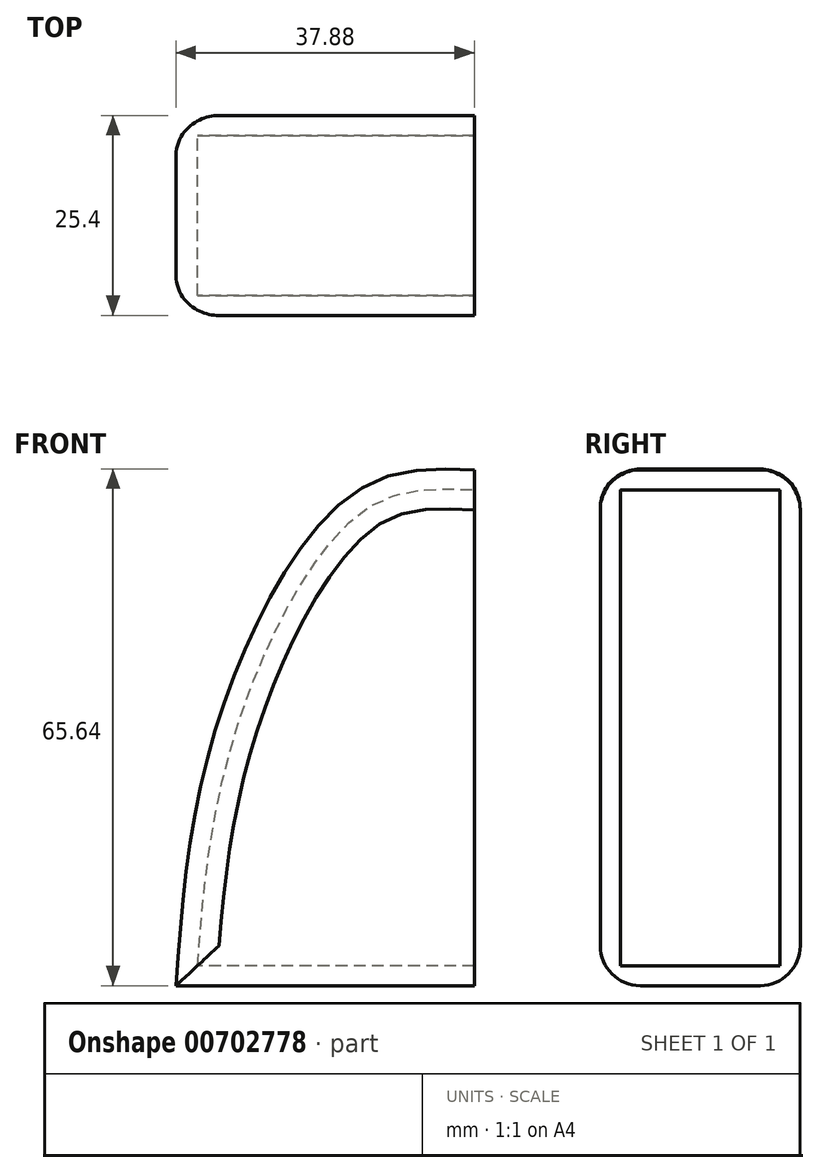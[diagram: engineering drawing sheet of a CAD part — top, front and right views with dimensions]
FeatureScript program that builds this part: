
annotation { "Feature Type Name" : "Feature", "Feature Type Description" : "" }
export const myFeature = defineFeature(function(context is Context, id is Id, definition is map)
    precondition{}
    {
        {
            var Q0;
            Q0=qCreatedBy(makeId("Front.planeOp"),FACE);
            var sketch = newSketch(context, id + "F0", { "sketchPlane" : qUnion([Q0])});
            skFitSpline(sketch, "E0", {"points": [v(0, 0) * mm, v(5.07, 32.72) * mm, v(22.58, 62.59) * mm, v(37.88, 65.54) * mm], "startDerivative": vector(6.12, 85.78) * mm, "endDerivative": vector(61.67, -2.48) * mm});
            skLineSegment(sketch, "E1", {"start": v(37.88, 65.54) * mm, "end": v(37.88, 0) * mm});
            skLineSegment(sketch, "E2", {"start": v(37.88, 0) * mm, "end": v(0, 0) * mm});
            skSolve(sketch);
        }
        {
            var Q0;
            Q0=makeQuery(id+"F0.imprint","IMPRINT",FACE,{"disambiguationData":[TD([[makeQuery(id+"F0.imprint","IMPRINT",EDGE,{"derivedFrom":sQuery(id+"F0.wireOp",EDGE,"E0")}),-1.0]])]});
            extrude(context, id + "F1", {"entities" : qUnion([Q0]), "depth" : 25.4 * mm, "offsetDistance" : 25.4 * mm});
        }
        {
            var Q0;
            Q0=makeQuery(id+"F1.opExtrude","SWEPT_FACE",FACE,{"disambiguationData":[OSD([sQuery(id+"F0.wireOp",EDGE,"E1")])]});
            shell(context, id + "F2", {"entities" : qUnion([Q0]), "thickness" : 2.54 * mm});
        }
        {
            var Q0;
            Q0=makeQuery(id+"F1.opExtrude","CAP_EDGE",EDGE,{"disambiguationData":[OSD([sQuery(id+"F0.wireOp",EDGE,"E0")])],"isStart":false});
            var Q1;
            Q1=makeQuery(id+"F1.opExtrude","CAP_EDGE",EDGE,{"disambiguationData":[OSD([sQuery(id+"F0.wireOp",EDGE,"E0")])],"isStart":true});
            var Q2;
            Q2=makeQuery(id+"F1.opExtrude","CAP_EDGE",EDGE,{"disambiguationData":[OSD([sQuery(id+"F0.wireOp",EDGE,"E2")])],"isStart":true});
            var Q3;
            Q3=makeQuery(id+"F1.opExtrude","CAP_EDGE",EDGE,{"disambiguationData":[OSD([sQuery(id+"F0.wireOp",EDGE,"E2")])],"isStart":false});
            fillet(context, id + "F3", {"entities" : qUnion([Q0, Q1, Q2, Q3]), "radius" : 5.08 * mm, "tangentPropagation" : true, "allowEdgeOverflow" : false});
        }
    });
